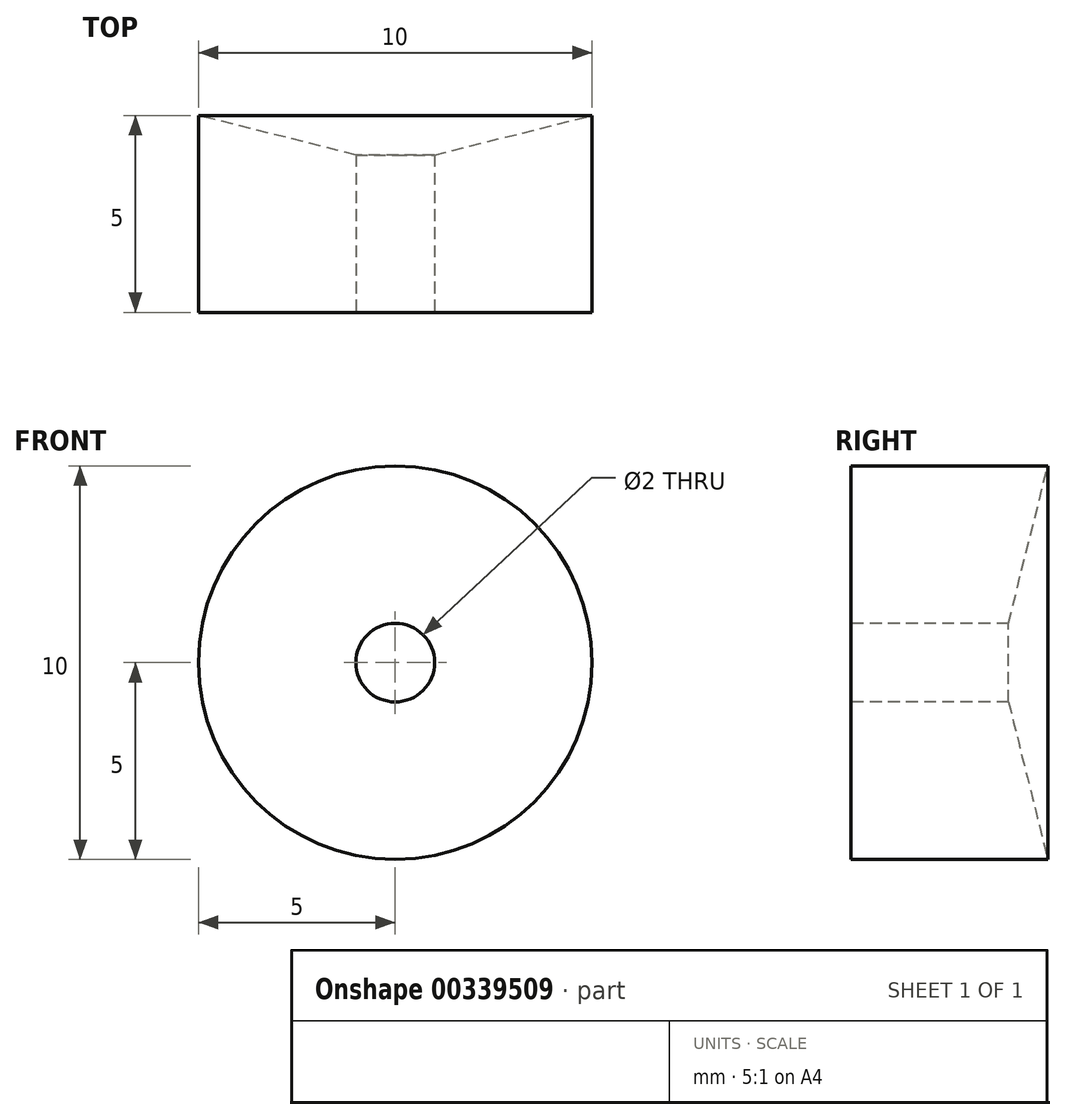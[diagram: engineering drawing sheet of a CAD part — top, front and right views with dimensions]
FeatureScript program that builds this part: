
annotation { "Feature Type Name" : "Feature", "Feature Type Description" : "" }
export const myFeature = defineFeature(function(context is Context, id is Id, definition is map)
    precondition{}
    {
        {
            var Q0;
            Q0=qCreatedBy(makeId("Right.planeOp"),FACE);
            var sketch = newSketch(context, id + "F0", { "sketchPlane" : qUnion([Q0])});
            skLineSegment(sketch, "E0.bottom", {"start": v(0, 0) * mm, "end": v(4, 0) * mm});
            skLineSegment(sketch, "E0.top", {"start": v(0, 5) * mm, "end": v(4, 5) * mm});
            skLineSegment(sketch, "E0.right", {"start": v(4, 0) * mm, "end": v(4, 5) * mm, "construction": true});
            skLineSegment(sketch, "E1", {"start": v(4, 5) * mm, "end": v(5, 5) * mm});
            skLineSegment(sketch, "E2", {"start": v(-30.07, 0) * mm, "end": v(24.6, 0) * mm, "construction": true});
            skLineSegment(sketch, "E3", {"start": v(0, 5) * mm, "end": v(0, 1) * mm});
            skLineSegment(sketch, "E4", {"start": v(0, 1) * mm, "end": v(4, 1) * mm});
            skLineSegment(sketch, "E5", {"start": v(4, 1) * mm, "end": v(5, 5) * mm});
            skSolve(sketch);
        }
        {
            var Q0;
            Q0=makeQuery(id+"F0.imprint","IMPRINT",FACE,{"disambiguationData":[TD([[makeQuery(id+"F0.imprint","IMPRINT",EDGE,{"derivedFrom":sQuery(id+"F0.wireOp",EDGE,"E0.top")}),-1.0]])]});
            var Q1;
            Q1=sQuery(id+"F0.wireOp",EDGE,"E2");
            revolve(context, id + "F1", {"entities" : qUnion([Q0]), "axis" : qUnion([Q1]), "revolveType" : RevolveType.FULL});
        }
    });
